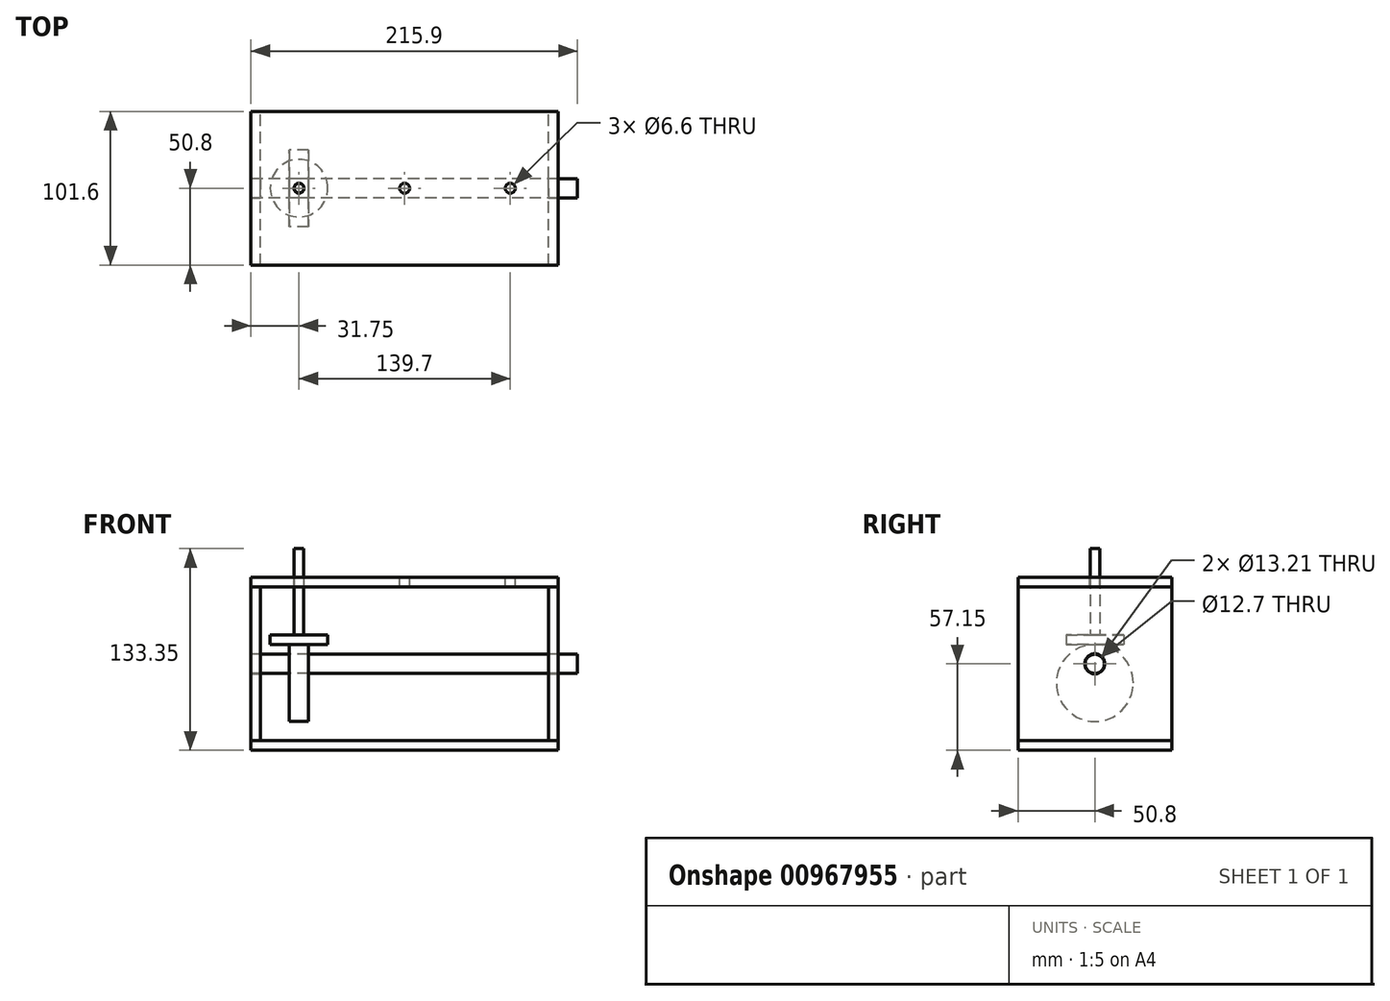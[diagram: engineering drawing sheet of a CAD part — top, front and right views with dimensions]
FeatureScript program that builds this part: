
annotation { "Feature Type Name" : "Feature", "Feature Type Description" : "" }
export const myFeature = defineFeature(function(context is Context, id is Id, definition is map)
    precondition{}
    {
        {
            var Q0;
            Q0=qCreatedBy(makeId("Front.planeOp"),FACE);
            var sketch = newSketch(context, id + "F0", { "sketchPlane" : qUnion([Q0])});
            skLineSegment(sketch, "E0.bottom", {"start": v(-101.6, 6.35) * mm, "end": v(101.6, 6.35) * mm});
            skLineSegment(sketch, "E0.top", {"start": v(-101.6, 0) * mm, "end": v(101.6, 0) * mm});
            skLineSegment(sketch, "E0.left", {"start": v(-101.6, 6.35) * mm, "end": v(-101.6, 0) * mm});
            skLineSegment(sketch, "E0.right", {"start": v(101.6, 6.35) * mm, "end": v(101.6, 0) * mm});
            skLineSegment(sketch, "E1", {"start": v(-101.6, 6.35) * mm, "end": v(-101.6, 107.95) * mm});
            skLineSegment(sketch, "E2", {"start": v(-101.6, 107.95) * mm, "end": v(101.6, 107.95) * mm});
            skLineSegment(sketch, "E3", {"start": v(101.6, 107.95) * mm, "end": v(101.6, 6.35) * mm});
            skLineSegment(sketch, "E4", {"start": v(-95.25, 6.35) * mm, "end": v(-95.25, 107.95) * mm});
            skLineSegment(sketch, "E5", {"start": v(95.25, 6.35) * mm, "end": v(95.25, 107.95) * mm});
            skLineSegment(sketch, "E6", {"start": v(-95.25, 57.15) * mm, "end": v(-101.6, 57.15) * mm, "construction": true});
            skLineSegment(sketch, "E7", {"start": v(95.25, 57.15) * mm, "end": v(101.6, 57.15) * mm, "construction": true});
            skLineSegment(sketch, "E8", {"start": v(-101.6, 107.95) * mm, "end": v(-101.6, 114.3) * mm});
            skLineSegment(sketch, "E9", {"start": v(-101.6, 114.3) * mm, "end": v(101.6, 114.3) * mm});
            skLineSegment(sketch, "E10", {"start": v(101.6, 114.3) * mm, "end": v(101.6, 107.95) * mm});
            skLineSegment(sketch, "E11", {"start": v(-95.25, 57.15) * mm, "end": v(-69.85, 57.15) * mm});
            skLineSegment(sketch, "E12", {"start": v(-69.85, 57.15) * mm, "end": v(0, 57.15) * mm});
            skLineSegment(sketch, "E13", {"start": v(0, 57.15) * mm, "end": v(69.85, 57.15) * mm});
            skLineSegment(sketch, "E14", {"start": v(69.85, 57.15) * mm, "end": v(95.25, 57.15) * mm});
            skLineSegment(sketch, "E15", {"start": v(-69.85, 57.15) * mm, "end": v(-69.85, 44.45) * mm, "construction": true});
            skLineSegment(sketch, "E16", {"start": v(0, 63.5) * mm, "end": v(0, 57.15) * mm, "construction": true});
            skLineSegment(sketch, "E17", {"start": v(69.85, 57.15) * mm, "end": v(69.85, 63.5) * mm, "construction": true});
            skLineSegment(sketch, "E18.bottom", {"start": v(-63.5, 69.85) * mm, "end": v(-76.2, 69.85) * mm});
            skLineSegment(sketch, "E18.top", {"start": v(-63.5, 19.05) * mm, "end": v(-76.2, 19.05) * mm});
            skLineSegment(sketch, "E18.left", {"start": v(-63.5, 69.85) * mm, "end": v(-63.5, 19.05) * mm});
            skLineSegment(sketch, "E18.right", {"start": v(-76.2, 69.85) * mm, "end": v(-76.2, 19.05) * mm});
            skPoint(sketch, "E18.middle", {"position": v(-69.85, 44.45) * mm});
            skLineSegment(sketch, "E19.bottom", {"start": v(6.35, 38.1) * mm, "end": v(-6.35, 38.1) * mm});
            skLineSegment(sketch, "E19.top", {"start": v(6.35, 88.9) * mm, "end": v(-6.35, 88.9) * mm});
            skLineSegment(sketch, "E19.left", {"start": v(6.35, 38.1) * mm, "end": v(6.35, 88.9) * mm});
            skLineSegment(sketch, "E19.right", {"start": v(-6.35, 38.1) * mm, "end": v(-6.35, 88.9) * mm});
            skPoint(sketch, "E19.middle", {"position": v(0, 63.5) * mm});
            skLineSegment(sketch, "E20.bottom", {"start": v(63.5, 38.1) * mm, "end": v(76.2, 38.1) * mm});
            skLineSegment(sketch, "E20.top", {"start": v(63.5, 88.9) * mm, "end": v(76.2, 88.9) * mm});
            skLineSegment(sketch, "E20.left", {"start": v(63.5, 38.1) * mm, "end": v(63.5, 88.9) * mm});
            skLineSegment(sketch, "E20.right", {"start": v(76.2, 38.1) * mm, "end": v(76.2, 88.9) * mm});
            skPoint(sketch, "E20.middle", {"position": v(69.85, 63.5) * mm});
            skLineSegment(sketch, "E21", {"start": v(-76.2, 44.45) * mm, "end": v(-63.5, 44.45) * mm});
            skLineSegment(sketch, "E22", {"start": v(-6.35, 63.5) * mm, "end": v(6.35, 63.5) * mm});
            skLineSegment(sketch, "E23", {"start": v(63.5, 63.5) * mm, "end": v(76.2, 63.5) * mm});
            skLineSegment(sketch, "E24", {"start": v(-69.85, 69.85) * mm, "end": v(-69.85, 133.35) * mm, "construction": true});
            skLineSegment(sketch, "E25", {"start": v(0, 88.9) * mm, "end": v(0, 152.4) * mm, "construction": true});
            skLineSegment(sketch, "E26", {"start": v(69.85, 88.9) * mm, "end": v(69.85, 152.4) * mm, "construction": true});
            skSolve(sketch);
        }
        {
            assignVariable(context, id + "F1", {"name" : "thickness", "anyValue" : 101.6 * mm});
        }
        {
            var Q0;
            Q0=makeQuery(id+"F0.imprint","IMPRINT",FACE,{"disambiguationData":[TD([[makeQuery(id+"F0.imprint","IMPRINT",EDGE,{"derivedFrom":sQuery(id+"F0.wireOp",EDGE,"E0.top")}),1.0]])]});
            var Q1;
            {var subQ0=sQuery(id+"F0.wireOp",EDGE,"E8");Q1=makeQuery(id+"F0.imprint","IMPRINT",FACE,{"disambiguationData":[TD([[makeQuery(id+"F0.imprint","IMPRINT",EDGE,{"derivedFrom":subQ0}),-1.0]])]});}
            extrude(context, id + "F2", {"entities" : qUnion([Q0, Q1]), "endBound" : BoundingType.SYMMETRIC, "depth" : getVariable(context, 'thickness'), "offsetDistance" : 25.4 * mm});
        }
        {
            var Q0;
            {var subQ1=sQuery(id+"F0.wireOp",EDGE,"E1");Q0=makeQuery(id+"F0.imprint","IMPRINT",FACE,{"disambiguationData":[TD([[makeQuery(id+"F0.imprint","IMPRINT",EDGE,{"derivedFrom":subQ1}),-1.0]])]});}
            var Q1;
            {var subQ4=sQuery(id+"F0.wireOp",EDGE,"E3");Q1=makeQuery(id+"F0.imprint","IMPRINT",FACE,{"disambiguationData":[TD([[makeQuery(id+"F0.imprint","IMPRINT",EDGE,{"derivedFrom":subQ4}),-1.0]])]});}
            var Q2;
            Q2=makeQuery(id+"F2.opExtrude","CAP_FACE",FACE,{"disambiguationData":[OSD([sQuery(id+"F0.wireOp",EDGE,"E2"),sQuery(id+"F0.wireOp",EDGE,"E8"),sQuery(id+"F0.wireOp",EDGE,"E9"),sQuery(id+"F0.wireOp",EDGE,"E10")])],"isStart":false});
            var Q3;
            Q3=makeQuery(id+"F2.opExtrude","CAP_FACE",FACE,{"disambiguationData":[OSD([sQuery(id+"F0.wireOp",EDGE,"E2"),sQuery(id+"F0.wireOp",EDGE,"E8"),sQuery(id+"F0.wireOp",EDGE,"E9"),sQuery(id+"F0.wireOp",EDGE,"E10")])],"isStart":true});
            extrude(context, id + "F3", {"entities" : qUnion([Q0, Q1]), "endBound" : BoundingType.UP_TO_SURFACE, "depth" : 25.4 * mm, "endBoundEntityFace" : qUnion([Q2]), "offsetDistance" : 25.4 * mm, "hasSecondDirection" : true, "secondDirectionBound" : SecondDirectionBoundingType.UP_TO_SURFACE, "secondDirectionOppositeDirection" : true, "secondDirectionDepth" : 25.4 * mm, "secondDirectionBoundEntityFace" : qUnion([Q3])});
        }
        {
            var Q0;
            Q0=makeQuery(id+"F3.opExtrude","SWEPT_FACE",FACE,{"disambiguationData":[OSD([sQuery(id+"F0.wireOp",EDGE,"E3")])]});
            var sketch = newSketch(context, id + "F4", { "sketchPlane" : qUnion([Q0])});
            skCircle(sketch, "E27", {"center": v(0, 57.15) * mm, "radius": 6.6 * mm});
            skCircle(sketch, "E28", {"center": v(0, 57.15) * mm, "radius": 6.35 * mm});
            skSolve(sketch);
        }
        {
            var Q0;
            Q0=makeQuery(id+"F4.imprint","IMPRINT",FACE,{"disambiguationData":[TD([[makeQuery(id+"F4.imprint","IMPRINT",EDGE,{"derivedFrom":sQuery(id+"F4.wireOp",EDGE,"E28")}),1.0]])]});
            var Q1;
            Q1=makeQuery(id+"F4.imprint","IMPRINT",FACE,{"disambiguationData":[TD([[makeQuery(id+"F4.imprint","IMPRINT",EDGE,{"derivedFrom":sQuery(id+"F4.wireOp",EDGE,"E27")}),1.0]])]});
            extrude(context, id + "F5", {"entities" : qUnion([Q0, Q1]), "operationType" : NewBodyOperationType.REMOVE, "endBound" : BoundingType.THROUGH_ALL, "oppositeDirection" : true, "depth" : 25.4 * mm, "offsetDistance" : 25.4 * mm});
        }
        {
            var Q0;
            Q0=makeQuery(id+"F4.imprint","IMPRINT",FACE,{"disambiguationData":[TD([[makeQuery(id+"F4.imprint","IMPRINT",EDGE,{"derivedFrom":sQuery(id+"F4.wireOp",EDGE,"E28")}),1.0]])]});
            var Q1;
            Q1=makeQuery(id+"F3.opExtrude","SWEPT_FACE",FACE,{"disambiguationData":[OSD([sQuery(id+"F0.wireOp",EDGE,"E1")])]});
            extrude(context, id + "F6", {"entities" : qUnion([Q0]), "depth" : 12.7 * mm, "offsetDistance" : 25.4 * mm, "hasSecondDirection" : true, "secondDirectionBound" : SecondDirectionBoundingType.UP_TO_SURFACE, "secondDirectionOppositeDirection" : true, "secondDirectionDepth" : 25.4 * mm, "secondDirectionBoundEntityFace" : qUnion([Q1])});
        }
        {
            var Q0;
            {var subQ0=sQuery(id+"F0.wireOp",EDGE,"E18.top");Q0=makeQuery(id+"F0.imprint","IMPRINT",FACE,{"disambiguationData":[TD([[makeQuery(id+"F0.imprint","IMPRINT",EDGE,{"derivedFrom":subQ0}),-1.0]])]});}
            var Q1;
            Q1=sQuery(id+"F0.wireOp",EDGE,"E21");
            revolve(context, id + "F7", {"surfaceOperationType" : NewSurfaceOperationType.NEW, "entities" : qUnion([Q0]), "axis" : qUnion([Q1]), "revolveType" : RevolveType.FULL});
        }
        {
            var Q0;
            Q0=makeQuery(id+"F6.opExtrude","SWEPT_BODY",BODY,{"disambiguationData":[OSD([sQuery(id+"F4.wireOp",EDGE,"E28")])]});
            var Q1;
            Q1=makeQuery(id+"F7.opRevolve","SWEPT_BODY",BODY,{"disambiguationData":[OSD([sQuery(id+"F0.wireOp",EDGE,"E18.top"),sQuery(id+"F0.wireOp",EDGE,"E18.left"),sQuery(id+"F0.wireOp",EDGE,"E18.right"),sQuery(id+"F0.wireOp",EDGE,"E21")])]});
            booleanBodies(context, id + "F8", {"operationType" : BooleanOperationType.SUBTRACTION, "tools" : qUnion([Q0]), "targets" : qUnion([Q1]), "keepTools" : true});
        }
        {
            var Q0;
            Q0=makeQuery(id+"F2.opExtrude","SWEPT_FACE",FACE,{"disambiguationData":[OSD([sQuery(id+"F0.wireOp",EDGE,"E9")])]});
            var sketch = newSketch(context, id + "F9", { "sketchPlane" : qUnion([Q0])});
            skPoint(sketch, "E29", {"position": v(-69.85, 0) * mm});
            skPoint(sketch, "E30", {"position": v(0, 0) * mm});
            skPoint(sketch, "E31", {"position": v(69.85, 0) * mm});
            skSolve(sketch);
        }
        {
            var Q0;
            Q0=sQuery(id+"F9.wireOp",VERTEX,"E29");
            var Q1;
            Q1=sQuery(id+"F9.wireOp",VERTEX,"E30");
            var Q2;
            Q2=sQuery(id+"F9.wireOp",VERTEX,"E31");
            var Q3;
            Q3=makeQuery(id+"F2.opExtrude","SWEPT_BODY",BODY,{"disambiguationData":[OSD([sQuery(id+"F0.wireOp",EDGE,"E2"),sQuery(id+"F0.wireOp",EDGE,"E8"),sQuery(id+"F0.wireOp",EDGE,"E9"),sQuery(id+"F0.wireOp",EDGE,"E10")])]});
            hole(context, id + "F10", {"style" : HoleStyle.SIMPLE, "endStyle" : HoleEndStyle.THROUGH, "holeDiameter" : 6.6 * mm, "majorDiameter" : 6.35 * mm, "isTappedThrough" : true, "tappedDepth" : 12.7 * mm, "tapClearance" : 3, "locations" : qUnion([Q0, Q1, Q2]), "scope" : qUnion([Q3])});
        }
        {
            var Q0;
            Q0=sQuery(id+"F0.wireOp",VERTEX,"E24.start");
            var Q1;
            Q1=qCreatedBy(makeId("Top.planeOp"),FACE);
            cPlane(context, id + "F11", {"entities" : qUnion([Q0, Q1]), "cplaneType" : CPlaneType.PLANE_POINT, "offset" : 25.4 * mm, "width" : 152.4 * mm, "height" : 152.4 * mm});
        }
        {
            var Q0;
            Q0=qCreatedBy(id+"F11.planeOp",FACE);
            var sketch = newSketch(context, id + "F12", { "sketchPlane" : qUnion([Q0])});
            skCircle(sketch, "E32", {"center": v(-69.85, 0) * mm, "radius": 3.18 * mm});
            skCircle(sketch, "E33", {"center": v(-69.85, 0) * mm, "radius": 19.05 * mm});
            skSolve(sketch);
        }
        {
            var Q0;
            Q0=makeQuery(id+"F12.imprint","IMPRINT",FACE,{"disambiguationData":[TD([[makeQuery(id+"F12.imprint","IMPRINT",EDGE,{"derivedFrom":sQuery(id+"F12.wireOp",EDGE,"E32")}),1.0]])]});
            var Q1;
            Q1=sQuery(id+"F12.wireOp",EDGE,"E32");
            var Q2;
            Q2=sQuery(id+"F0.wireOp",VERTEX,"E24.end");
            extrude(context, id + "F13", {"entities" : qUnion([Q0]), "surfaceEntities" : qUnion([Q1]), "endBound" : BoundingType.UP_TO_VERTEX, "depth" : 25.4 * mm, "endBoundEntityVertex" : qUnion([Q2]), "offsetDistance" : 25.4 * mm});
        }
        {
            var Q0;
            Q0=makeQuery(id+"F12.imprint","IMPRINT",FACE,{"disambiguationData":[TD([[makeQuery(id+"F12.imprint","IMPRINT",EDGE,{"derivedFrom":sQuery(id+"F12.wireOp",EDGE,"E32")}),-1.0]])]});
            var Q1;
            Q1=sQuery(id+"F12.wireOp",EDGE,"E33");
            extrude(context, id + "F14", {"entities" : qUnion([Q0]), "operationType" : NewBodyOperationType.ADD, "surfaceEntities" : qUnion([Q1]), "depth" : 6.35 * mm, "offsetDistance" : 25.4 * mm});
        }
    });
